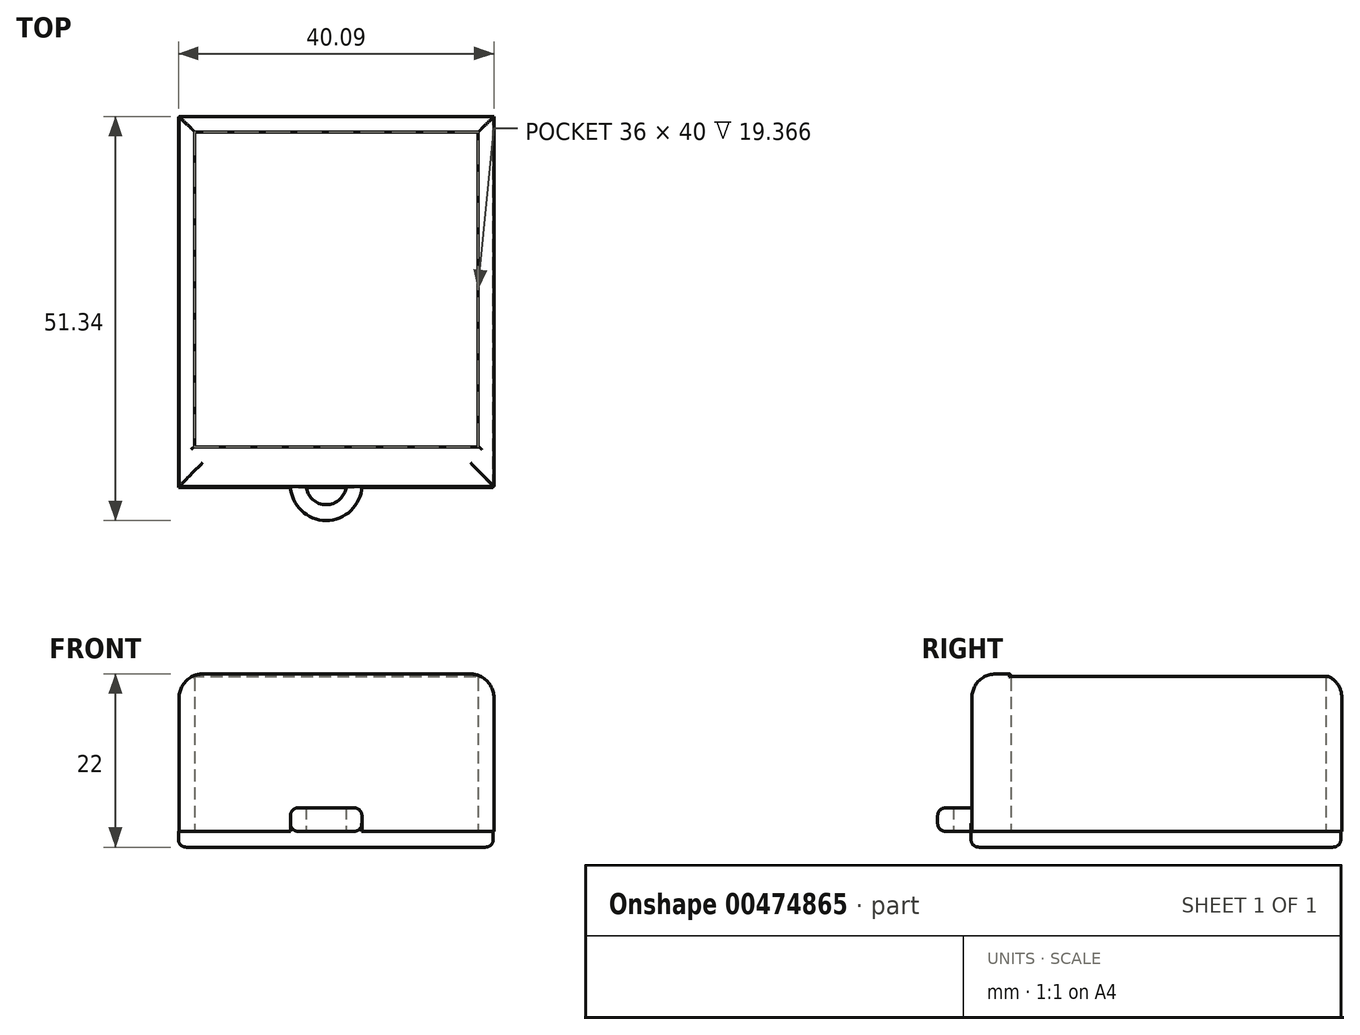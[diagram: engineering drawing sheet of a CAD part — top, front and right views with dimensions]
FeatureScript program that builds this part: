
annotation { "Feature Type Name" : "Feature", "Feature Type Description" : "" }
export const myFeature = defineFeature(function(context is Context, id is Id, definition is map)
    precondition{}
    {
        {
            var Q0;
            Q0=qCreatedBy(makeId("Top.planeOp"),FACE);
            var sketch = newSketch(context, id + "F0", { "sketchPlane" : qUnion([Q0])});
            skLineSegment(sketch, "E0.bottom", {"start": v(-40, 13.47) * mm, "end": v(0, 13.47) * mm});
            skLineSegment(sketch, "E0.top", {"start": v(-40, -33.53) * mm, "end": v(0, -33.53) * mm});
            skLineSegment(sketch, "E0.left", {"start": v(-40, 13.47) * mm, "end": v(-40, -33.53) * mm});
            skLineSegment(sketch, "E0.right", {"start": v(0, 13.47) * mm, "end": v(0, -33.53) * mm});
            skLineSegment(sketch, "E1.0", {"start": v(-38, 11.47) * mm, "end": v(-38, -28.53) * mm});
            skLineSegment(sketch, "E2.0", {"start": v(-38, 11.47) * mm, "end": v(-2, 11.47) * mm});
            skLineSegment(sketch, "E3.0", {"start": v(-2, 11.47) * mm, "end": v(-2, -28.53) * mm});
            skLineSegment(sketch, "E4.0", {"start": v(-38, -28.53) * mm, "end": v(-2, -28.53) * mm});
            skSolve(sketch);
        }
        {
            var Q0;
            Q0=makeQuery(id+"F0.imprint","IMPRINT",FACE,{"disambiguationData":[TD([[makeQuery(id+"F0.imprint","IMPRINT",EDGE,{"derivedFrom":sQuery(id+"F0.wireOp",EDGE,"E0.bottom")}),-1.0]])]});
            extrude(context, id + "F1", {"entities" : qUnion([Q0]), "depth" : 20 * mm});
        }
        {
            var Q0;
            Q0=makeQuery(id+"F1.opExtrude","CAP_FACE",FACE,{"disambiguationData":[OSD([sQuery(id+"F0.wireOp",EDGE,"E0.bottom"),sQuery(id+"F0.wireOp",EDGE,"E0.top"),sQuery(id+"F0.wireOp",EDGE,"E0.left"),sQuery(id+"F0.wireOp",EDGE,"E0.right"),sQuery(id+"F0.wireOp",EDGE,"E1.0"),sQuery(id+"F0.wireOp",EDGE,"E2.0"),sQuery(id+"F0.wireOp",EDGE,"E3.0"),sQuery(id+"F0.wireOp",EDGE,"E4.0")])],"isStart":true});
            cPlane(context, id + "F2", {"entities" : qUnion([Q0]), "cplaneType" : CPlaneType.OFFSET, "offset" : 0 * mm, "width" : 150 * mm, "height" : 150 * mm});
        }
        {
            var Q0;
            Q0=qCreatedBy(id+"F2.planeOp",FACE);
            var sketch = newSketch(context, id + "F3", { "sketchPlane" : qUnion([Q0])});
            skLineSegment(sketch, "E5.bottom", {"start": v(-40.09, 33.65) * mm, "end": v(-0.09, 33.65) * mm});
            skLineSegment(sketch, "E5.top", {"start": v(-40.09, -13.35) * mm, "end": v(-0.09, -13.35) * mm});
            skLineSegment(sketch, "E5.left", {"start": v(-40.09, 33.65) * mm, "end": v(-40.09, -13.35) * mm});
            skLineSegment(sketch, "E5.right", {"start": v(-0.09, 33.65) * mm, "end": v(-0.09, -13.35) * mm});
            skSolve(sketch);
        }
        {
            var Q0;
            Q0=makeQuery(id+"F3.imprint","IMPRINT",FACE,{"disambiguationData":[TD([[makeQuery(id+"F3.imprint","IMPRINT",EDGE,{"derivedFrom":sQuery(id+"F3.wireOp",EDGE,"f675def1-d90f-45a8-83b3-6b41bb0a4f13.bottom")}),-1.0]])]});
            var Q1;
            Q1=makeQuery(id+"F3.imprint","IMPRINT",FACE,{"disambiguationData":[TD([[makeQuery(id+"F3.imprint","IMPRINT",EDGE,{"derivedFrom":sQuery(id+"F3.wireOp",EDGE,"E5.bottom")}),-1.0]])]});
            extrude(context, id + "F4", {"entities" : qUnion([Q0, Q1]), "operationType" : NewBodyOperationType.ADD, "depth" : 2 * mm});
        }
        {
            var Q0;
            Q0=qCreatedBy(makeId("Top.planeOp"),FACE);
            var sketch = newSketch(context, id + "F5", { "sketchPlane" : qUnion([Q0])});
            skArc(sketch, "E6", {"start": v(-25.85, -33.33) * mm, "mid": v(-20.73, -37.83) * mm, "end": v(-16.93, -32.16) * mm});
            skPoint(sketch, "E7.end.orphan", {"position": v(-21.32, -37.7) * mm});
            skPoint(sketch, "E8.end.orphan", {"position": v(-16.26, -33.33) * mm});
            skArc(sketch, "E9.0", {"start": v(-23.85, -33.33) * mm, "mid": v(-20.99, -35.85) * mm, "end": v(-18.86, -32.68) * mm});
            skLineSegment(sketch, "E10", {"start": v(-25.85, -33.33) * mm, "end": v(-23.85, -33.33) * mm});
            skLineSegment(sketch, "E11", {"start": v(-18.86, -32.68) * mm, "end": v(-16.93, -32.16) * mm});
            skSolve(sketch);
        }
        {
            var Q0;
            Q0=makeQuery(id+"F5.imprint","IMPRINT",FACE,{"disambiguationData":[TD([[makeQuery(id+"F5.imprint","IMPRINT",EDGE,{"derivedFrom":sQuery(id+"F5.wireOp",EDGE,"E6")}),1.0]])]});
            extrude(context, id + "F6", {"entities" : qUnion([Q0]), "operationType" : NewBodyOperationType.ADD, "depth" : 3 * mm});
        }
        {
            var Q0;
            Q0=makeQuery(id+"F1.opExtrude","CAP_EDGE",EDGE,{"disambiguationData":[OSD([sQuery(id+"F0.wireOp",EDGE,"E0.left")])],"isStart":false});
            var Q1;
            Q1=makeQuery(id+"F1.opExtrude","CAP_EDGE",EDGE,{"disambiguationData":[OSD([sQuery(id+"F0.wireOp",EDGE,"E0.right")])],"isStart":false});
            var Q2;
            Q2=makeQuery(id+"F4.opExtrude","CAP_EDGE",EDGE,{"disambiguationData":[OSD([sQuery(id+"F3.wireOp",EDGE,"f675def1-d90f-45a8-83b3-6b41bb0a4f13.left")])],"isStart":false});
            var Q3;
            Q3=makeQuery(id+"F4.opExtrude","CAP_EDGE",EDGE,{"disambiguationData":[OSD([sQuery(id+"F3.wireOp",EDGE,"f675def1-d90f-45a8-83b3-6b41bb0a4f13.top")])],"isStart":false});
            var Q4;
            Q4=makeQuery(id+"F4.opExtrude","CAP_EDGE",EDGE,{"disambiguationData":[OSD([sQuery(id+"F3.wireOp",EDGE,"f675def1-d90f-45a8-83b3-6b41bb0a4f13.right")])],"isStart":false});
            var Q5;
            Q5=makeQuery(id+"F1.opExtrude","CAP_EDGE",EDGE,{"disambiguationData":[OSD([sQuery(id+"F0.wireOp",EDGE,"E0.bottom")])],"isStart":false});
            var Q6;
            Q6=makeQuery(id+"F1.opExtrude","CAP_EDGE",EDGE,{"disambiguationData":[OSD([sQuery(id+"F0.wireOp",EDGE,"E0.top")])],"isStart":false});
            fillet(context, id + "F7", {"entities" : qUnion([Q0, Q1, Q2, Q3, Q4, Q5, Q6]), "radius" : 3 * mm, "tangentPropagation" : true, "allowEdgeOverflow" : false});
        }
        {
            var Q0;
            Q0=makeQuery(id+"F4.boolean.opBoolean","SPLIT",FACE,{"disambiguationData":[TD([makeQuery(id+"F1.opExtrude","SWEPT_FACE",FACE,{"disambiguationData":[OSD([sQuery(id+"F0.wireOp",EDGE,"E1.0")])]})])],"derivedFrom":makeQuery(id+"F4.opExtrude","CAP_FACE",FACE,{"disambiguationData":[OSD([sQuery(id+"F3.wireOp",EDGE,"f675def1-d90f-45a8-83b3-6b41bb0a4f13.bottom"),sQuery(id+"F3.wireOp",EDGE,"f675def1-d90f-45a8-83b3-6b41bb0a4f13.top"),sQuery(id+"F3.wireOp",EDGE,"f675def1-d90f-45a8-83b3-6b41bb0a4f13.left"),sQuery(id+"F3.wireOp",EDGE,"f675def1-d90f-45a8-83b3-6b41bb0a4f13.right")])],"isStart":true})});
            var Q1;
            Q1=makeQuery(id+"F6.opExtrude","CAP_EDGE",EDGE,{"disambiguationData":[OSD([sQuery(id+"F5.wireOp",EDGE,"E6")])],"isStart":false});
            var Q2;
            {var subQ0=sQuery(id+"F5.wireOp",EDGE,"E6");Q2=makeQuery(id+"F6.boolean.opBoolean","SPLIT",EDGE,{"disambiguationData":[topologyDisambiguationEdgeConnected([makeQuery(id+"F6.opExtrude","SWEPT_FACE",FACE,{"disambiguationData":[OSD([subQ0])]}),makeQuery(id+"F6.opExtrude","CAP_FACE",FACE,{"disambiguationData":[OSD([subQ0,sQuery(id+"F5.wireOp",EDGE,"E9.0"),sQuery(id+"F5.wireOp",EDGE,"E10"),sQuery(id+"F5.wireOp",EDGE,"E11")])],"isStart":true})])],"derivedFrom":makeQuery(id+"F6.opExtrude","CAP_EDGE",EDGE,{"disambiguationData":[OSD([subQ0])],"isStart":true})});}
            var Q3;
            Q3=makeQuery(id+"F4.opExtrude","CAP_FACE",FACE,{"disambiguationData":[OSD([sQuery(id+"F3.wireOp",EDGE,"E5.bottom"),sQuery(id+"F3.wireOp",EDGE,"E5.top"),sQuery(id+"F3.wireOp",EDGE,"E5.left"),sQuery(id+"F3.wireOp",EDGE,"E5.right")])],"isStart":false});
            fillet(context, id + "F8", {"entities" : qUnion([Q0, Q1, Q2, Q3]), "radius" : 1 * mm, "tangentPropagation" : true, "allowEdgeOverflow" : false});
        }
        {
            var Q0;
            Q0=makeQuery(id+"F7.opFillet","BLEND_EDGE",EDGE,{"blendedFrom":[makeQuery(id+"F1.opExtrude","CAP_EDGE",EDGE,{"disambiguationData":[OSD([sQuery(id+"F0.wireOp",EDGE,"E0.left")])],"isStart":false}),makeQuery(id+"F1.opExtrude","SWEPT_FACE",FACE,{"disambiguationData":[OSD([sQuery(id+"F0.wireOp",EDGE,"E1.0")])]})],"blendedInto":[makeQuery(id+"F1.opExtrude","SWEPT_FACE",FACE,{"disambiguationData":[OSD([sQuery(id+"F0.wireOp",EDGE,"E1.0")])]})]});
            var Q1;
            Q1=makeQuery(id+"F1.opExtrude","CAP_EDGE",EDGE,{"disambiguationData":[OSD([sQuery(id+"F0.wireOp",EDGE,"E4.0")])],"isStart":false});
            var Q2;
            Q2=makeQuery(id+"F7.opFillet","BLEND_EDGE",EDGE,{"blendedFrom":[makeQuery(id+"F1.opExtrude","CAP_EDGE",EDGE,{"disambiguationData":[OSD([sQuery(id+"F0.wireOp",EDGE,"E0.right")])],"isStart":false}),makeQuery(id+"F1.opExtrude","SWEPT_FACE",FACE,{"disambiguationData":[OSD([sQuery(id+"F0.wireOp",EDGE,"E3.0")])]})],"blendedInto":[makeQuery(id+"F1.opExtrude","SWEPT_FACE",FACE,{"disambiguationData":[OSD([sQuery(id+"F0.wireOp",EDGE,"E3.0")])]})]});
            var Q3;
            Q3=makeQuery(id+"F7.opFillet","BLEND_EDGE",EDGE,{"blendedFrom":[makeQuery(id+"F1.opExtrude","CAP_EDGE",EDGE,{"disambiguationData":[OSD([sQuery(id+"F0.wireOp",EDGE,"E0.bottom")])],"isStart":false}),makeQuery(id+"F1.opExtrude","SWEPT_FACE",FACE,{"disambiguationData":[OSD([sQuery(id+"F0.wireOp",EDGE,"E2.0")])]})],"blendedInto":[makeQuery(id+"F1.opExtrude","SWEPT_FACE",FACE,{"disambiguationData":[OSD([sQuery(id+"F0.wireOp",EDGE,"E2.0")])]})]});
            fillet(context, id + "F9", {"entities" : qUnion([Q0, Q1, Q2, Q3]), "radius" : 0.3 * mm, "tangentPropagation" : true, "allowEdgeOverflow" : false});
        }
    });
